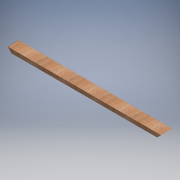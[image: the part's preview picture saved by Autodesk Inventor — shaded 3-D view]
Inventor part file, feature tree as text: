
AUTODESK INVENTOR PART (.ipt)
format: ipt  version: 2016 (Build 200138000, 138)  size: 99,840 bytes
history: native  units: in
note: dims shown in document units (in); Inventor stores cm internally (conversion verified against a paired STEP export)
features: extrude x1, sketch x1
ambient origin geometry x8: Origin, YZ Plane, XZ Plane, XY Plane, X Axis, Y Axis, Z Axis, Center Point
bodies: Body1 (feature_tree)
feature tree (2):
  extrude  "Extrusion2"  TaperAngle=135.0deg  [1 undecoded]
  sketch  "Sketch2"  dims[d10=45.0deg d11=135.0deg d12=3.5in d13=0.0in d14=48.25in d15=1.5in]
note: 1 required parameter value undecoded (feature->parameter linkage not recoverable at this tier; creation-order binding heuristic only, values carry confidence <= 0.55)
